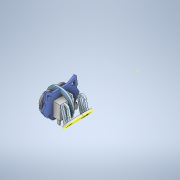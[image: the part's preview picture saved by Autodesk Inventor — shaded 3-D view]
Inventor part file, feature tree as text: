
AUTODESK INVENTOR PART (.ipt)
format: ipt  version: 2020.3 (Build 243373000, 373)  size: 4,048,384 bytes
history: native  units: mm
features: other x83, direct_edit x1, sketch x1
ambient origin geometry x8: Origin, YZ Plane, XZ Plane, XY Plane, X Axis, Y Axis, Z Axis, Center Point
bodies: Solid1 (feature_tree), Solid2 (feature_tree), Solid3 (feature_tree), Solid4 (feature_tree), Solid5 (feature_tree), Solid6 (feature_tree), Solid7 (feature_tree), Solid8 (feature_tree), Solid9 (feature_tree), Solid10 (feature_tree), Solid11 (feature_tree), Solid12 (feature_tree), Solid13 (feature_tree), Solid14 (feature_tree), Solid15 (feature_tree), Solid16 (feature_tree), Solid17 (feature_tree), Solid18 (feature_tree), Solid19 (feature_tree), Solid20 (feature_tree), Solid21 (feature_tree), Solid22 (feature_tree), Solid23 (feature_tree), Solid24 (feature_tree), Solid25 (feature_tree), Solid26 (feature_tree), Solid27 (feature_tree), Solid28 (feature_tree), Solid29 (feature_tree), Solid30 (feature_tree), Solid31 (feature_tree), Solid32 (feature_tree), Solid33 (feature_tree), Solid34 (feature_tree), Solid35 (feature_tree), Solid36 (feature_tree), Solid37 (feature_tree), Solid38 (feature_tree), Solid39 (feature_tree), Solid40 (feature_tree), Solid41 (feature_tree), Solid42 (feature_tree), Solid43 (feature_tree), Solid44 (feature_tree), Solid45 (feature_tree), Solid46 (feature_tree), Solid47 (feature_tree), Solid48 (feature_tree), Solid49 (feature_tree), Solid50 (feature_tree), Solid51 (feature_tree), Solid52 (feature_tree), Solid53 (feature_tree), Solid54 (feature_tree), Solid55 (feature_tree), Solid56 (feature_tree), Solid57 (feature_tree), Solid58 (feature_tree), Solid59 (feature_tree), Solid60 (feature_tree), Solid61 (feature_tree), Solid62 (feature_tree), Solid63 (feature_tree), Solid64 (feature_tree), Solid65 (feature_tree), Solid66 (feature_tree), Solid67 (feature_tree), Solid68 (feature_tree), Solid69 (feature_tree), Solid70 (feature_tree), Solid71 (feature_tree), Solid72 (feature_tree), Solid73 (feature_tree), Solid74 (feature_tree), Solid75 (feature_tree), Solid76 (feature_tree), Solid77 (feature_tree), Solid78 (feature_tree), Solid79 (feature_tree), Solid80 (feature_tree), Solid81 (feature_tree)
feature tree (85):
  other  "head _1_.iam"
  other  "Brophy HC-SR04-UltrasonicSensor _1_.iam:1::HC-SR04-UltrasonicSensor v7.ipt:1"
  other  "Brophy HC-SR04-UltrasonicSensor _1_.iam:1::HC-SR04-UltrasonicSensor v7_1.ipt:1"
  other  "Brophy HC-SR04-UltrasonicSensor _1_.iam:1::HC-SR04-UltrasonicSensor v7_2.ipt:1"
  other  "Brophy HC-SR04-UltrasonicSensor _1_.iam:1::HC-SR04-UltrasonicSensor v7_3.ipt:1"
  other  "Brophy HC-SR04-UltrasonicSensor _1_.iam:1::HC-SR04-UltrasonicSensor v7_4.ipt:1"
  other  "Brophy HC-SR04-UltrasonicSensor _1_.iam:1::HC-SR04-UltrasonicSensor v7_5.ipt:1"
  other  "Brophy HC-SR04-UltrasonicSensor _1_.iam:1::HC-SR04-UltrasonicSensor v7_6.ipt:1"
  other  "Brophy HC-SR04-UltrasonicSensor _1_.iam:1::HC-SR04-UltrasonicSensor v7_7.ipt:1"
  other  "Brophy HC-SR04-UltrasonicSensor _1_.iam:1::HC-SR04-UltrasonicSensor v7_8.ipt:1"
  other  "Brophy HC-SR04-UltrasonicSensor _1_.iam:1::HC-SR04-UltrasonicSensor v7_9.ipt:1"
  other  "Brophy HC-SR04-UltrasonicSensor _1_.iam:1::Part 72.ipt:1"
  other  "Brophy HC-SR04-UltrasonicSensor _1_.iam:1::HC-SR04-UltrasonicSensor v7_10.ipt:1"
  other  "Brophy HC-SR04-UltrasonicSensor _1_.iam:1::HC-SR04-UltrasonicSensor v7_11.ipt:1"
  other  "Brophy HC-SR04-UltrasonicSensor _1_.iam:1::Part 70.ipt:1"
  other  "Brophy HC-SR04-UltrasonicSensor _1_.iam:1::HC-SR04-UltrasonicSensor v7_12.ipt:1"
  other  "Brophy HC-SR04-UltrasonicSensor _1_.iam:1::HC-SR04-UltrasonicSensor v7_13.ipt:1"
  other  "Brophy HC-SR04-UltrasonicSensor _1_.iam:1::HC-SR04-UltrasonicSensor v7_14.ipt:1"
  other  "Brophy HC-SR04-UltrasonicSensor _1_.iam:1::HC-SR04-UltrasonicSensor v7_15.ipt:1"
  other  "Brophy HC-SR04-UltrasonicSensor _1_.iam:1::HC-SR04-UltrasonicSensor v7_16.ipt:1"
  other  "Brophy HC-SR04-UltrasonicSensor _1_.iam:1::HC-SR04-UltrasonicSensor v7_17.ipt:1"
  other  "Brophy HC-SR04-UltrasonicSensor _1_.iam:1::HC-SR04-UltrasonicSensor v7_18.ipt:1"
  other  "Brophy HC-SR04-UltrasonicSensor _1_.iam:1::HC-SR04-UltrasonicSensor v7_19.ipt:1"
  other  "Brophy HC-SR04-UltrasonicSensor _1_.iam:1::Part 68.ipt:1"
  other  "Brophy HC-SR04-UltrasonicSensor _1_.iam:1::HC-SR04-UltrasonicSensor v7_20.ipt:1"
  other  "Brophy HC-SR04-UltrasonicSensor _1_.iam:1::HC-SR04-UltrasonicSensor v7_21.ipt:1"
  other  "Brophy HC-SR04-UltrasonicSensor _1_.iam:1::HC-SR04-UltrasonicSensor v7_22.ipt:1"
  other  "Brophy HC-SR04-UltrasonicSensor _1_.iam:1::HC-SR04-UltrasonicSensor v7_23.ipt:1"
  other  "Brophy HC-SR04-UltrasonicSensor _1_.iam:1::Part 62.ipt:1"
  other  "Brophy HC-SR04-UltrasonicSensor _1_.iam:1::HC-SR04-UltrasonicSensor v7_24.ipt:1"
  other  "Brophy HC-SR04-UltrasonicSensor _1_.iam:1::HC-SR04-UltrasonicSensor v7_25.ipt:1"
  other  "Brophy HC-SR04-UltrasonicSensor _1_.iam:1::HC-SR04-UltrasonicSensor v7_26.ipt:1"
  other  "Brophy HC-SR04-UltrasonicSensor _1_.iam:1::Part 58.ipt:1"
  other  "Brophy HC-SR04-UltrasonicSensor _1_.iam:1::Part 63.ipt:1"
  other  "Brophy HC-SR04-UltrasonicSensor _1_.iam:1::HC-SR04-UltrasonicSensor v7_27.ipt:1"
  other  "Brophy HC-SR04-UltrasonicSensor _1_.iam:1::HC-SR04-UltrasonicSensor v7_28.ipt:1"
  other  "Brophy HC-SR04-UltrasonicSensor _1_.iam:1::Part 69.ipt:1"
  other  "Brophy HC-SR04-UltrasonicSensor _1_.iam:1::Part 67.ipt:1"
  other  "Brophy HC-SR04-UltrasonicSensor _1_.iam:1::HC-SR04-UltrasonicSensor v7_29.ipt:1"
  other  "Brophy HC-SR04-UltrasonicSensor _1_.iam:1::Part 64.ipt:1"
  other  "Brophy HC-SR04-UltrasonicSensor _1_.iam:1::HC-SR04-UltrasonicSensor v7_30.ipt:1"
  other  "Brophy HC-SR04-UltrasonicSensor _1_.iam:1::HC-SR04-UltrasonicSensor v7_31.ipt:1"
  other  "Brophy HC-SR04-UltrasonicSensor _1_.iam:1::Part 65.ipt:1"
  other  "Brophy HC-SR04-UltrasonicSensor _1_.iam:1::HC-SR04-UltrasonicSensor v7_32.ipt:1"
  other  "Brophy HC-SR04-UltrasonicSensor _1_.iam:1::HC-SR04-UltrasonicSensor v7_33.ipt:1"
  other  "Brophy HC-SR04-UltrasonicSensor _1_.iam:1::Part 61.ipt:1"
  other  "Brophy HC-SR04-UltrasonicSensor _1_.iam:1::HC-SR04-UltrasonicSensor v7_34.ipt:1"
  other  "Brophy HC-SR04-UltrasonicSensor _1_.iam:1::HC-SR04-UltrasonicSensor v7_35.ipt:1"
  other  "Brophy HC-SR04-UltrasonicSensor _1_.iam:1::HC-SR04-UltrasonicSensor v7_36.ipt:1"
  other  "Brophy HC-SR04-UltrasonicSensor _1_.iam:1::HC-SR04-UltrasonicSensor v7_37.ipt:1"
  other  "Brophy HC-SR04-UltrasonicSensor _1_.iam:1::HC-SR04-UltrasonicSensor v7_38.ipt:1"
  other  "Brophy HC-SR04-UltrasonicSensor _1_.iam:1::HC-SR04-UltrasonicSensor v7_39.ipt:1"
  other  "Brophy HC-SR04-UltrasonicSensor _1_.iam:1::HC-SR04-UltrasonicSensor v7_40.ipt:1"
  other  "Brophy HC-SR04-UltrasonicSensor _1_.iam:1::HC-SR04-UltrasonicSensor v7_41.ipt:1"
  other  "Brophy HC-SR04-UltrasonicSensor _1_.iam:1::HC-SR04-UltrasonicSensor v7_42.ipt:1"
  other  "Brophy HC-SR04-UltrasonicSensor _1_.iam:1::Part 71.ipt:1"
  other  "Brophy HC-SR04-UltrasonicSensor _1_.iam:1::HC-SR04-UltrasonicSensor v7_43.ipt:1"
  other  "Brophy HC-SR04-UltrasonicSensor _1_.iam:1::HC-SR04-UltrasonicSensor v7_44.ipt:1"
  other  "Brophy HC-SR04-UltrasonicSensor _1_.iam:1::Part 66.ipt:1"
  other  "Brophy HC-SR04-UltrasonicSensor _1_.iam:1::HC-SR04-UltrasonicSensor v7_45.ipt:1"
  other  "Brophy HC-SR04-UltrasonicSensor _1_.iam:1::HC-SR04-UltrasonicSensor v7_46.ipt:1"
  other  "Brophy HC-SR04-UltrasonicSensor _1_.iam:1::HC-SR04-UltrasonicSensor v7_47.ipt:1"
  other  "Brophy HC-SR04-UltrasonicSensor _1_.iam:1::Part 59.ipt:1"
  other  "Brophy HC-SR04-UltrasonicSensor _1_.iam:1::HC-SR04-UltrasonicSensor v7_48.ipt:1"
  other  "Brophy HC-SR04-UltrasonicSensor _1_.iam:1::Part 60.ipt:1"
  other  "Brophy HC-SR04-UltrasonicSensor _1_.iam:1::HC-SR04-UltrasonicSensor v7_49.ipt:1"
  other  "Brophy HC-SR04-UltrasonicSensor _1_.iam:1::HC-SR04-UltrasonicSensor v7_50.ipt:1"
  other  "Brophy HC-SR04-UltrasonicSensor _1_.iam:1::HC-SR04-UltrasonicSensor v7_51.ipt:1"
  other  "Brophy HC-SR04-UltrasonicSensor _1_.iam:1::HC-SR04-UltrasonicSensor v7_52.ipt:1"
  other  "Brophy HC-SR04-UltrasonicSensor _1_.iam:1::HC-SR04-UltrasonicSensor v7_53.ipt:1"
  other  "Brophy HC-SR04-UltrasonicSensor _1_.iam:1::HC-SR04-UltrasonicSensor v7_54.ipt:1"
  other  "Brophy HC-SR04-UltrasonicSensor _1_.iam:1::HC-SR04-UltrasonicSensor v7_55.ipt:1"
  other  "Brophy HC-SR04-UltrasonicSensor _1_.iam:1::HC-SR04-UltrasonicSensor v7_56.ipt:1"
  other  "Part 12.ipt:1"
  other  "Part 1.ipt:1"
  other  "Part 1_1.ipt:1"
  other  "Part 5.ipt:1"
  other  "Part 3.ipt:1"
  other  "Part 13.ipt:1"
  other  "Part 4.ipt:1"
  other  "Part 2.ipt:1"
  other  "Part 13.ipt:2"
  direct_edit  "Direct Edit1"
  sketch  "Sketch1"  dims[d0=20.0mm d1=4.0mm]
  other  "Size1"
